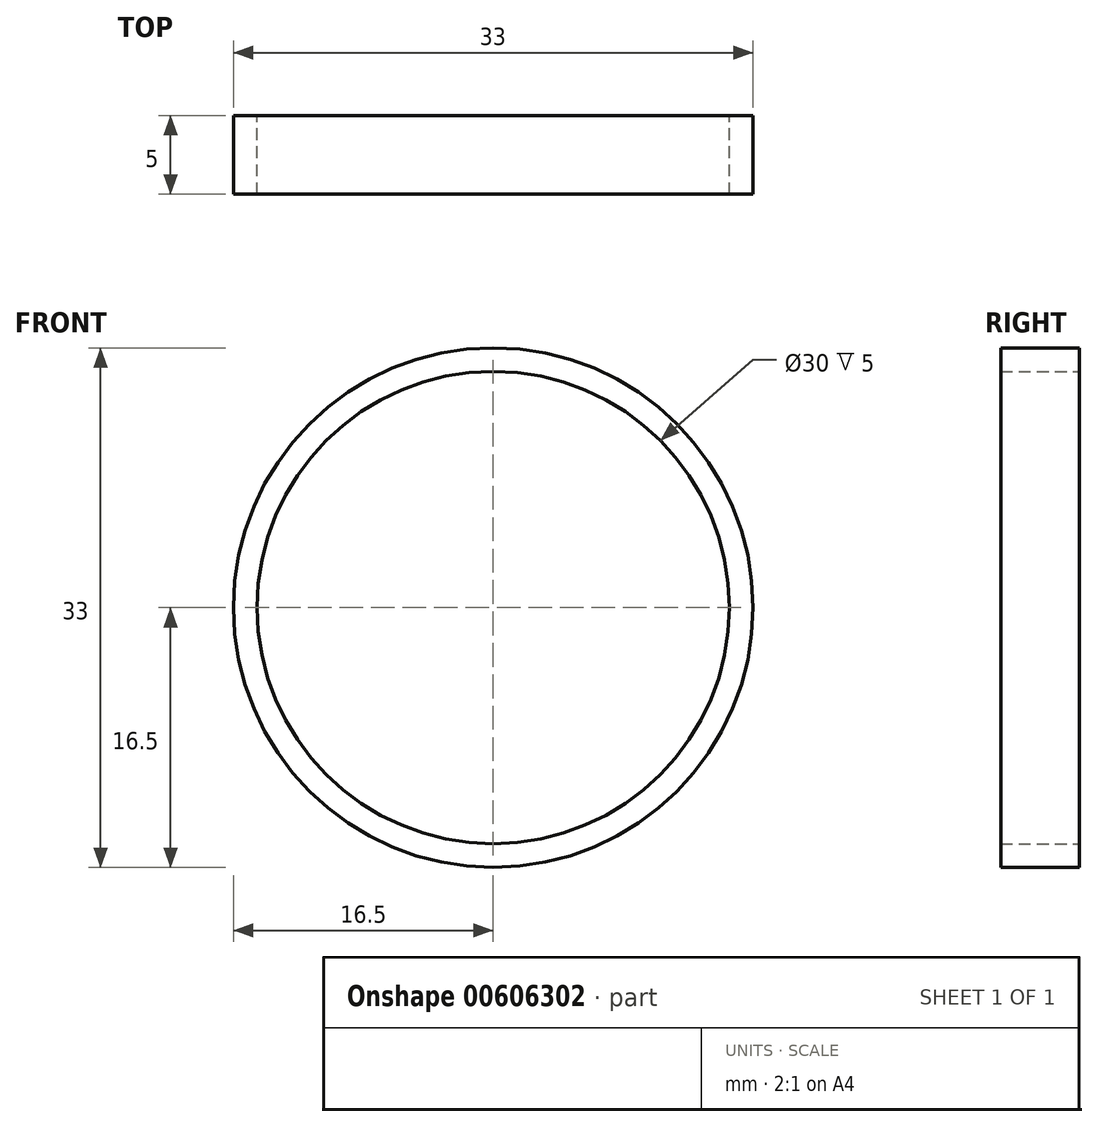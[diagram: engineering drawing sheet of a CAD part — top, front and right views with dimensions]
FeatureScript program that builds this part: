
annotation { "Feature Type Name" : "Feature", "Feature Type Description" : "" }
export const myFeature = defineFeature(function(context is Context, id is Id, definition is map)
    precondition{}
    {
        {
            var Q0;
            Q0=qCreatedBy(makeId("Front.planeOp"),FACE);
            var sketch = newSketch(context, id + "F0", { "sketchPlane" : qUnion([Q0])});
            skCircle(sketch, "E0", {"center": v(0, 0) * mm, "radius": 15 * mm});
            skCircle(sketch, "E1", {"center": v(0, 0) * mm, "radius": 16.5 * mm});
            skSolve(sketch);
        }
        {
            var Q0;
            Q0=makeQuery(id+"F0.imprint","IMPRINT",FACE,{"disambiguationData":[TD([[makeQuery(id+"F0.imprint","IMPRINT",EDGE,{"derivedFrom":sQuery(id+"F0.wireOp",EDGE,"E0")}),-1.0]])]});
            extrude(context, id + "F1", {"entities" : qUnion([Q0]), "depth" : 5 * mm, "offsetDistance" : 25 * mm});
        }
    });
